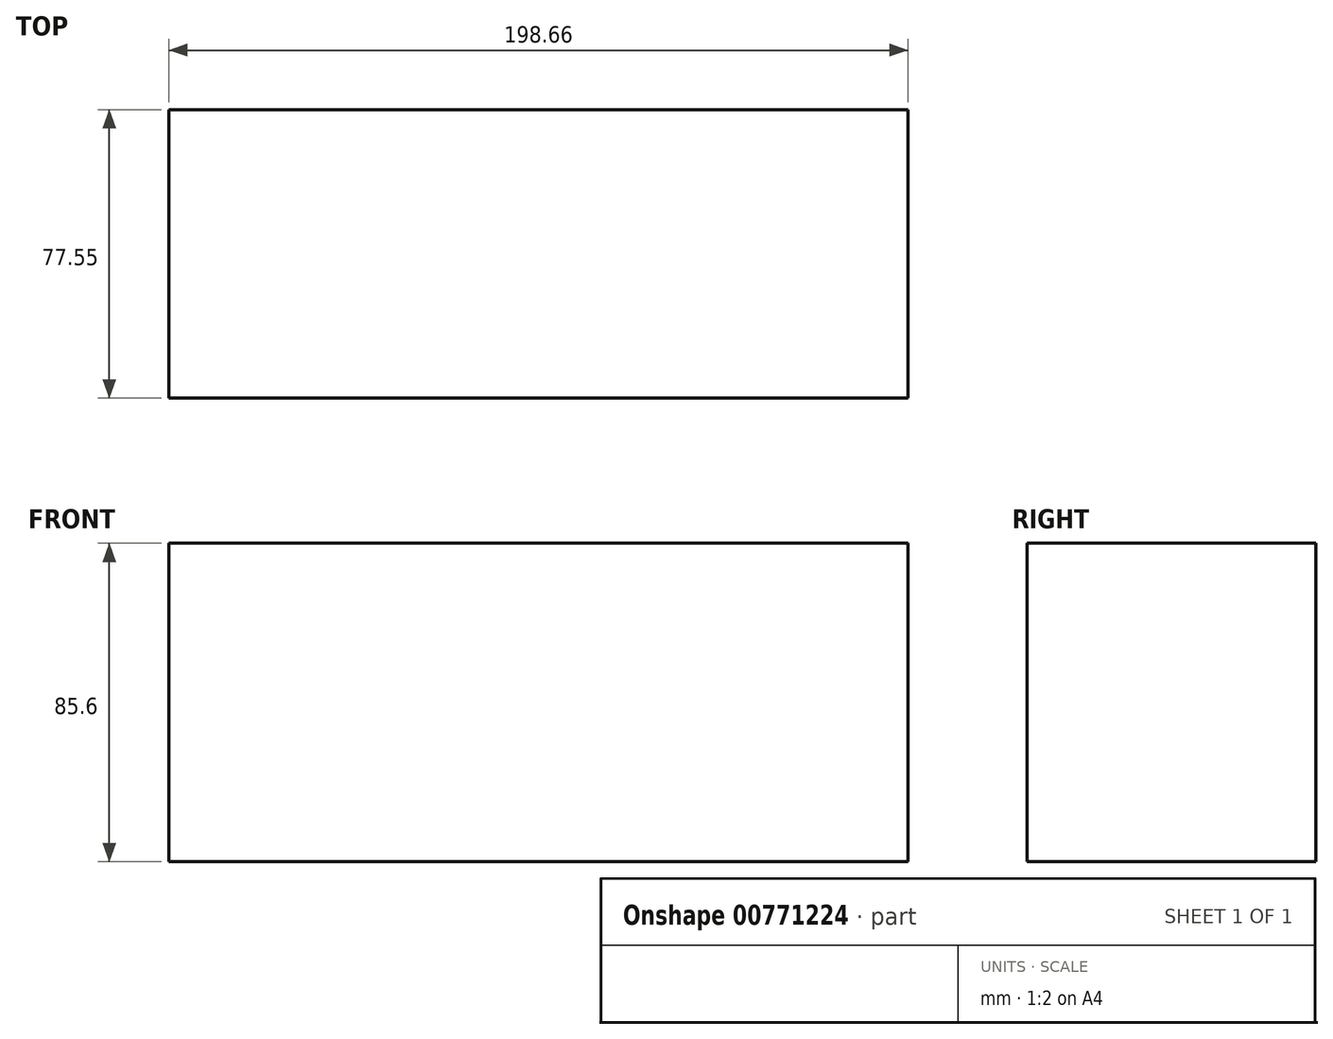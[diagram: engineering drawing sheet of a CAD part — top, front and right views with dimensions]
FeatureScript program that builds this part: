
annotation { "Feature Type Name" : "Feature", "Feature Type Description" : "" }
export const myFeature = defineFeature(function(context is Context, id is Id, definition is map)
    precondition{}
    {
        {
            var Q0;
            Q0=qCreatedBy(makeId("Top.planeOp"),FACE);
            var sketch = newSketch(context, id + "F0", { "sketchPlane" : qUnion([Q0])});
            skLineSegment(sketch, "E0.bottom", {"start": v(-112.18, 13.25) * mm, "end": v(86.48, 13.25) * mm});
            skLineSegment(sketch, "E0.top", {"start": v(-112.18, -64.3) * mm, "end": v(86.48, -64.3) * mm});
            skLineSegment(sketch, "E0.left", {"start": v(-112.18, 13.25) * mm, "end": v(-112.18, -64.3) * mm});
            skLineSegment(sketch, "E0.right", {"start": v(86.48, 13.25) * mm, "end": v(86.48, -64.3) * mm});
            skSolve(sketch);
        }
        {
            var Q0;
            Q0=makeQuery(id+"F0.imprint","IMPRINT",FACE,{"disambiguationData":[TD([[makeQuery(id+"F0.imprint","IMPRINT",EDGE,{"derivedFrom":sQuery(id+"F0.wireOp",EDGE,"E0.bottom")}),-1.0]])]});
            extrude(context, id + "F1", {"entities" : qUnion([Q0]), "depth" : 85.6 * mm, "offsetDistance" : 25.4 * mm});
        }
    });
